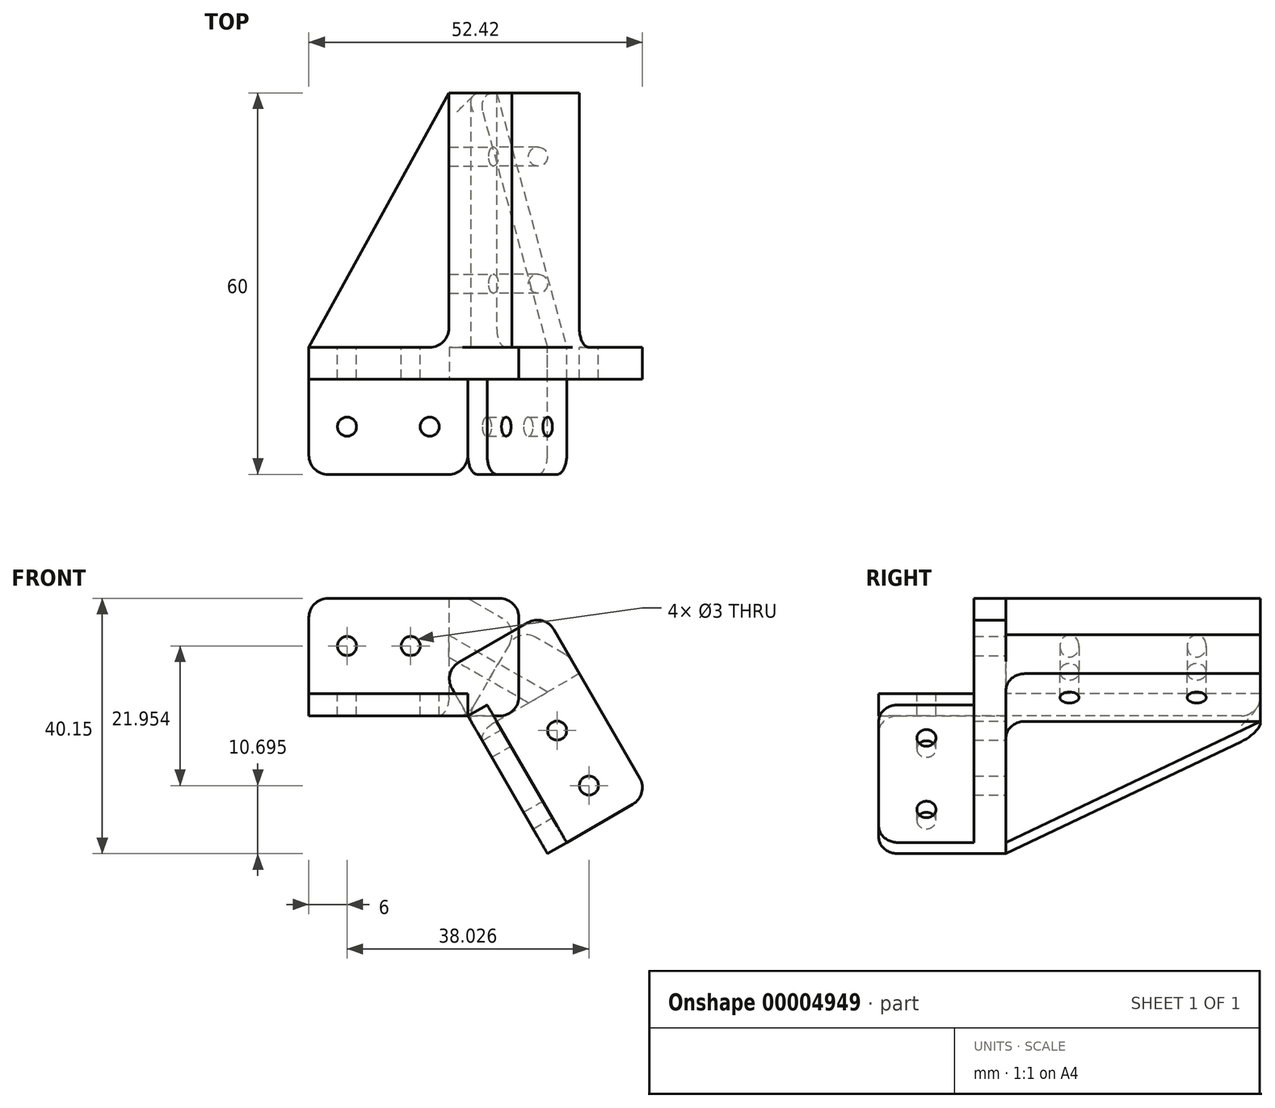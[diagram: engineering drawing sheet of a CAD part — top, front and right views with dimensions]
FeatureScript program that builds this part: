
annotation { "Feature Type Name" : "Feature", "Feature Type Description" : "" }
export const myFeature = defineFeature(function(context is Context, id is Id, definition is map)
    precondition{}
    {
        {
            var Q0;
            Q0=qCreatedBy(makeId("Top.planeOp"),FACE);
            var sketch = newSketch(context, id + "F0", { "sketchPlane" : qUnion([Q0])});
            skLineSegment(sketch, "E0", {"start": v(0, 0) * mm, "end": v(25, 0) * mm});
            skLineSegment(sketch, "E1", {"start": v(25, 0) * mm, "end": v(25, 45) * mm});
            skLineSegment(sketch, "E2", {"start": v(25, 45) * mm, "end": v(22, 45) * mm});
            skLineSegment(sketch, "E3", {"start": v(22, 45) * mm, "end": v(22, 5) * mm});
            skLineSegment(sketch, "E4", {"start": v(22, 5) * mm, "end": v(0, 5) * mm});
            skLineSegment(sketch, "E5", {"start": v(0, 5) * mm, "end": v(0, 0) * mm});
            skSolve(sketch);
        }
        {
            var Q0;
            Q0 = qSketchRegion(id + "F0", true);
            extrude(context, id + "F1", {"entities" : qUnion([Q0]), "depth" : 15 * mm, "symmetric" : true});
        }
        {
            var Q0;
            Q0=makeQuery(id+"F1.opExtrude","CAP_FACE",FACE,{"disambiguationData":[OSD([sQuery(id+"F0.wireOp",EDGE,"E0"),sQuery(id+"F0.wireOp",EDGE,"E1"),sQuery(id+"F0.wireOp",EDGE,"E2"),sQuery(id+"F0.wireOp",EDGE,"E3"),sQuery(id+"F0.wireOp",EDGE,"E4"),sQuery(id+"F0.wireOp",EDGE,"E5")])],"isStart":true});
            var sketch = newSketch(context, id + "F2", { "sketchPlane" : qUnion([Q0])});
            skLineSegment(sketch, "E6.0", {"start": v(25, 0) * mm, "end": v(25, -45) * mm});
            skLineSegment(sketch, "E6.1", {"start": v(25, -45) * mm, "end": v(22, -45) * mm});
            skLineSegment(sketch, "E6.2", {"start": v(0, -5) * mm, "end": v(0, 0) * mm});
            skLineSegment(sketch, "E7", {"start": v(22, -45) * mm, "end": v(0, -5) * mm});
            skLineSegment(sketch, "E8", {"start": v(25, 0) * mm, "end": v(25, 15) * mm});
            skLineSegment(sketch, "E9", {"start": v(25, 15) * mm, "end": v(0, 15) * mm});
            skLineSegment(sketch, "E10", {"start": v(0, 15) * mm, "end": v(0, 0) * mm});
            skSolve(sketch);
        }
        {
            var Q0;
            Q0 = qSketchRegion(id + "F2", true);
            extrude(context, id + "F3", {"entities" : qUnion([Q0]), "operationType" : NewBodyOperationType.ADD, "depth" : 3.5 * mm});
        }
        {
            var Q0;
            Q0=makeQuery(id+"F3.boolean.opBoolean","MERGE",FACE,{"derivedFrom":[makeQuery(id+"F1.opExtrude","SWEPT_FACE",FACE,{"disambiguationData":[OSD([sQuery(id+"F0.wireOp",EDGE,"E2")])]}),makeQuery(id+"F3.opExtrude","SWEPT_FACE",FACE,{"disambiguationData":[OSD([sQuery(id+"F2.wireOp",EDGE,"E6.1")])]})]});
            var sketch = newSketch(context, id + "F4", { "sketchPlane" : qUnion([Q0])});
            skLineSegment(sketch, "E11", {"start": v(-25, -11) * mm, "end": v(-25, 7.5) * mm});
            skLineSegment(sketch, "E12", {"start": v(-25, 7.5) * mm, "end": v(-33.01, 2.88) * mm});
            skLineSegment(sketch, "E13", {"start": v(-33.01, 2.88) * mm, "end": v(-25, -11) * mm});
            skSolve(sketch);
        }
        {
            var Q0;
            Q0 = qSketchRegion(id + "F4", true);
            var Q1;
            Q1=makeQuery(id+"F1.opExtrude","SWEPT_FACE",FACE,{"disambiguationData":[OSD([sQuery(id+"F0.wireOp",EDGE,"E0")])]});
            extrude(context, id + "F5", {"entities" : qUnion([Q0]), "operationType" : NewBodyOperationType.ADD, "endBound" : BoundingType.UP_TO_SURFACE, "oppositeDirection" : true, "endBoundEntityFace" : qUnion([Q1]), "depth" : 25 * mm});
        }
        {
            var Q0;
            Q0=makeQuery(id+"F1.opExtrude","SWEPT_FACE",FACE,{"disambiguationData":[OSD([sQuery(id+"F0.wireOp",EDGE,"E4")])]});
            var sketch = newSketch(context, id + "F6", { "sketchPlane" : qUnion([Q0])});
            skLineSegment(sketch, "E14", {"start": v(-22, 0) * mm, "end": v(0, 0) * mm, "construction": true});
            skLineSegment(sketch, "E15", {"start": v(-11, 0) * mm, "end": v(-11, 7.5) * mm, "construction": true});
            skCircle(sketch, "E16", {"center": v(-16, 0) * mm, "radius": 1.5 * mm});
            skCircle(sketch, "E17.0.MirrorC", {"center": v(-6, 0) * mm, "radius": 1.5 * mm});
            skSolve(sketch);
        }
        {
            var Q0;
            Q0 = qSketchRegion(id + "F6", true);
            extrude(context, id + "F7", {"entities" : qUnion([Q0]), "operationType" : NewBodyOperationType.REMOVE, "endBound" : BoundingType.THROUGH_ALL, "oppositeDirection" : true, "depth" : 25 * mm});
        }
        {
            var Q0;
            {var subQ0=sQuery(id+"F2.wireOp",EDGE,"E6.0");var subQ1=sQuery(id+"F2.wireOp",EDGE,"E6.2");var subQ2=sQuery(id+"F2.wireOp",EDGE,"E8");var subQ3=sQuery(id+"F2.wireOp",EDGE,"E9");var subQ4=sQuery(id+"F2.wireOp",EDGE,"E10");Q0=makeQuery(id+"F3.boolean.opBoolean","SPLIT",FACE,{"disambiguationData":[TD([makeQuery(id+"F1.opExtrude","SWEPT_FACE",FACE,{"disambiguationData":[OSD([sQuery(id+"F0.wireOp",EDGE,"E0")])]})])],"derivedFrom":makeQuery(id+"F3.opExtrude","CAP_FACE",FACE,{"disambiguationData":[OSD([subQ0,sQuery(id+"F2.wireOp",EDGE,"E6.1"),subQ1,sQuery(id+"F2.wireOp",EDGE,"E7"),subQ2,subQ3,subQ4])],"isStart":true})});}
            var sketch = newSketch(context, id + "F8", { "sketchPlane" : qUnion([Q0])});
            skLineSegment(sketch, "E18", {"start": v(0, -7.5) * mm, "end": v(25, -7.5) * mm, "construction": true});
            skLineSegment(sketch, "E19", {"start": v(12.5, -7.5) * mm, "end": v(12.5, -15) * mm, "construction": true});
            skCircle(sketch, "E20", {"center": v(6, -7.5) * mm, "radius": 1.5 * mm});
            skCircle(sketch, "E21.0.MirrorC", {"center": v(19, -7.5) * mm, "radius": 1.5 * mm});
            skSolve(sketch);
        }
        {
            var Q0;
            Q0 = qSketchRegion(id + "F8", true);
            extrude(context, id + "F9", {"entities" : qUnion([Q0]), "operationType" : NewBodyOperationType.REMOVE, "endBound" : BoundingType.THROUGH_ALL, "oppositeDirection" : true, "depth" : 25 * mm});
        }
        {
            var Q0;
            Q0=makeQuery(id+"F5.opExtrude","SWEPT_FACE",FACE,{"disambiguationData":[OSD([sQuery(id+"F4.wireOp",EDGE,"E13")])]});
            var sketch = newSketch(context, id + "F10", { "sketchPlane" : qUnion([Q0])});
            skLineSegment(sketch, "E22.0", {"start": v(5, 17.5) * mm, "end": v(5, 4.5) * mm, "construction": true});
            skLineSegment(sketch, "E23", {"start": v(5, 11) * mm, "end": v(45, 11) * mm, "construction": true});
            skLineSegment(sketch, "E24", {"start": v(25, 11) * mm, "end": v(25, 19) * mm, "construction": true});
            skCircle(sketch, "E25", {"center": v(35, 11) * mm, "radius": 1.5 * mm});
            skCircle(sketch, "E26.0.MirrorC", {"center": v(15, 11) * mm, "radius": 1.5 * mm});
            skSolve(sketch);
        }
        {
            var Q0;
            Q0 = qSketchRegion(id + "F10", true);
            extrude(context, id + "F11", {"entities" : qUnion([Q0]), "operationType" : NewBodyOperationType.REMOVE, "endBound" : BoundingType.THROUGH_ALL, "oppositeDirection" : true, "depth" : 25 * mm});
        }
        {
            var Q0;
            Q0=makeQuery(id+"F5.boolean.opBoolean","MERGE",FACE,{"derivedFrom":[makeQuery(id+"F1.opExtrude","SWEPT_FACE",FACE,{"disambiguationData":[OSD([sQuery(id+"F0.wireOp",EDGE,"E0")])]}),makeQuery(id+"F5.opExtrude","CAP_FACE",FACE,{"disambiguationData":[OSD([sQuery(id+"F4.wireOp",EDGE,"E11"),sQuery(id+"F4.wireOp",EDGE,"E12"),sQuery(id+"F4.wireOp",EDGE,"E13")])],"isStart":false})]});
            var sketch = newSketch(context, id + "F12", { "sketchPlane" : qUnion([Q0])});
            skLineSegment(sketch, "E27.bottom", {"start": v(25, -11) * mm, "end": v(33.01, -11) * mm});
            skLineSegment(sketch, "E27.top", {"start": v(25, 7.5) * mm, "end": v(33.01, 7.5) * mm});
            skLineSegment(sketch, "E27.left", {"start": v(25, -11) * mm, "end": v(25, 7.5) * mm});
            skLineSegment(sketch, "E27.right", {"start": v(33.01, -11) * mm, "end": v(33.01, 7.5) * mm});
            skSolve(sketch);
        }
        {
            var Q0;
            Q0 = qSketchRegion(id + "F12", true);
            var Q1;
            Q1=makeQuery(id+"F1.opExtrude","SWEPT_FACE",FACE,{"disambiguationData":[OSD([sQuery(id+"F0.wireOp",EDGE,"E4")])]});
            extrude(context, id + "F13", {"entities" : qUnion([Q0]), "operationType" : NewBodyOperationType.ADD, "endBound" : BoundingType.UP_TO_SURFACE, "oppositeDirection" : true, "endBoundEntityFace" : qUnion([Q1]), "depth" : 25 * mm});
        }
        {
            var Q0;
            Q0=makeQuery(id+"F1.opExtrude","SWEPT_EDGE",EDGE,{"disambiguationData":[OSD([sQuery(id+"F0.wireOp",EDGE,"E3"),sQuery(id+"F0.wireOp",EDGE,"E4")])]});
            var Q1;
            Q1=makeQuery(id+"F1.opExtrude","CAP_EDGE",EDGE,{"disambiguationData":[OSD([sQuery(id+"F0.wireOp",EDGE,"E5")])],"isStart":false});
            var Q2;
            Q2=makeQuery(id+"F3.opExtrude","SWEPT_EDGE",EDGE,{"disambiguationData":[OSD([sQuery(id+"F2.wireOp",EDGE,"E9"),sQuery(id+"F2.wireOp",EDGE,"E10")])]});
            var Q3;
            Q3=makeQuery(id+"F3.opExtrude","SWEPT_EDGE",EDGE,{"disambiguationData":[OSD([sQuery(id+"F2.wireOp",EDGE,"E8"),sQuery(id+"F2.wireOp",EDGE,"E9")])]});
            var Q4;
            Q4=makeQuery(id+"F5.opExtrude","SWEPT_EDGE",EDGE,{"disambiguationData":[OSD([sQuery(id+"F4.wireOp",EDGE,"E12"),sQuery(id+"F4.wireOp",EDGE,"E13")])]});
            var Q5;
            Q5=makeQuery(id+"F5.boolean.opBoolean","MERGE",EDGE,{"derivedFrom":[makeQuery(id+"F1.opExtrude","CAP_EDGE",EDGE,{"disambiguationData":[OSD([sQuery(id+"F0.wireOp",EDGE,"E1")])],"isStart":false}),makeQuery(id+"F5.opExtrude","SWEPT_EDGE",EDGE,{"disambiguationData":[OSD([sQuery(id+"F0.wireOp",EDGE,"E2"),sQuery(id+"F4.wireOp",EDGE,"E11"),sQuery(id+"F4.wireOp",EDGE,"E12")])]})]});
            var Q6;
            Q6=makeQuery(id+"F3.opExtrude","CAP_EDGE",EDGE,{"disambiguationData":[OSD([sQuery(id+"F2.wireOp",EDGE,"E6.1")])],"isStart":false});
            var Q7;
            Q7=makeQuery(id+"F5.boolean.opBoolean","MERGE",EDGE,{"derivedFrom":[makeQuery(id+"F3.opExtrude","CAP_EDGE",EDGE,{"disambiguationData":[OSD([sQuery(id+"F2.wireOp",EDGE,"E6.0"),sQuery(id+"F2.wireOp",EDGE,"E8")])],"isStart":false}),makeQuery(id+"F5.opExtrude","SWEPT_EDGE",EDGE,{"disambiguationData":[OSD([sQuery(id+"F2.wireOp",EDGE,"E6.1"),sQuery(id+"F4.wireOp",EDGE,"E11"),sQuery(id+"F4.wireOp",EDGE,"E13")])]})]});
            var Q8;
            Q8=makeQuery(id+"F13.opExtrude","SWEPT_EDGE",EDGE,{"disambiguationData":[OSD([sQuery(id+"F12.wireOp",EDGE,"E27.top"),sQuery(id+"F12.wireOp",EDGE,"E27.right")])]});
            var Q9;
            Q9=makeQuery(id+"F13.opExtrude","SWEPT_EDGE",EDGE,{"disambiguationData":[OSD([sQuery(id+"F12.wireOp",EDGE,"E27.bottom"),sQuery(id+"F12.wireOp",EDGE,"E27.right")])]});
            fillet(context, id + "F14", {"entities" : qUnion([Q0, Q1, Q2, Q3, Q4, Q5, Q6, Q7, Q8, Q9]), "radius" : 3 * mm, "tangentPropagation" : true, "allowEdgeOverflow" : false});
        }
        {
            var Q0;
            Q0=makeQuery(id+"F1.opExtrude","SWEPT_BODY",BODY,{"disambiguationData":[OSD([sQuery(id+"F0.wireOp",EDGE,"E0"),sQuery(id+"F0.wireOp",EDGE,"E1"),sQuery(id+"F0.wireOp",EDGE,"E2"),sQuery(id+"F0.wireOp",EDGE,"E3"),sQuery(id+"F0.wireOp",EDGE,"E4"),sQuery(id+"F0.wireOp",EDGE,"E5")])]});
            var Q1;
            Q1=makeQuery(id+"F5.opExtrude","SWEPT_FACE",FACE,{"disambiguationData":[OSD([sQuery(id+"F4.wireOp",EDGE,"E13")])]});
            mirror(context, id + "F15", {"entities" : qUnion([Q0]), "mirrorPlane" : qUnion([Q1])});
        }
    });
